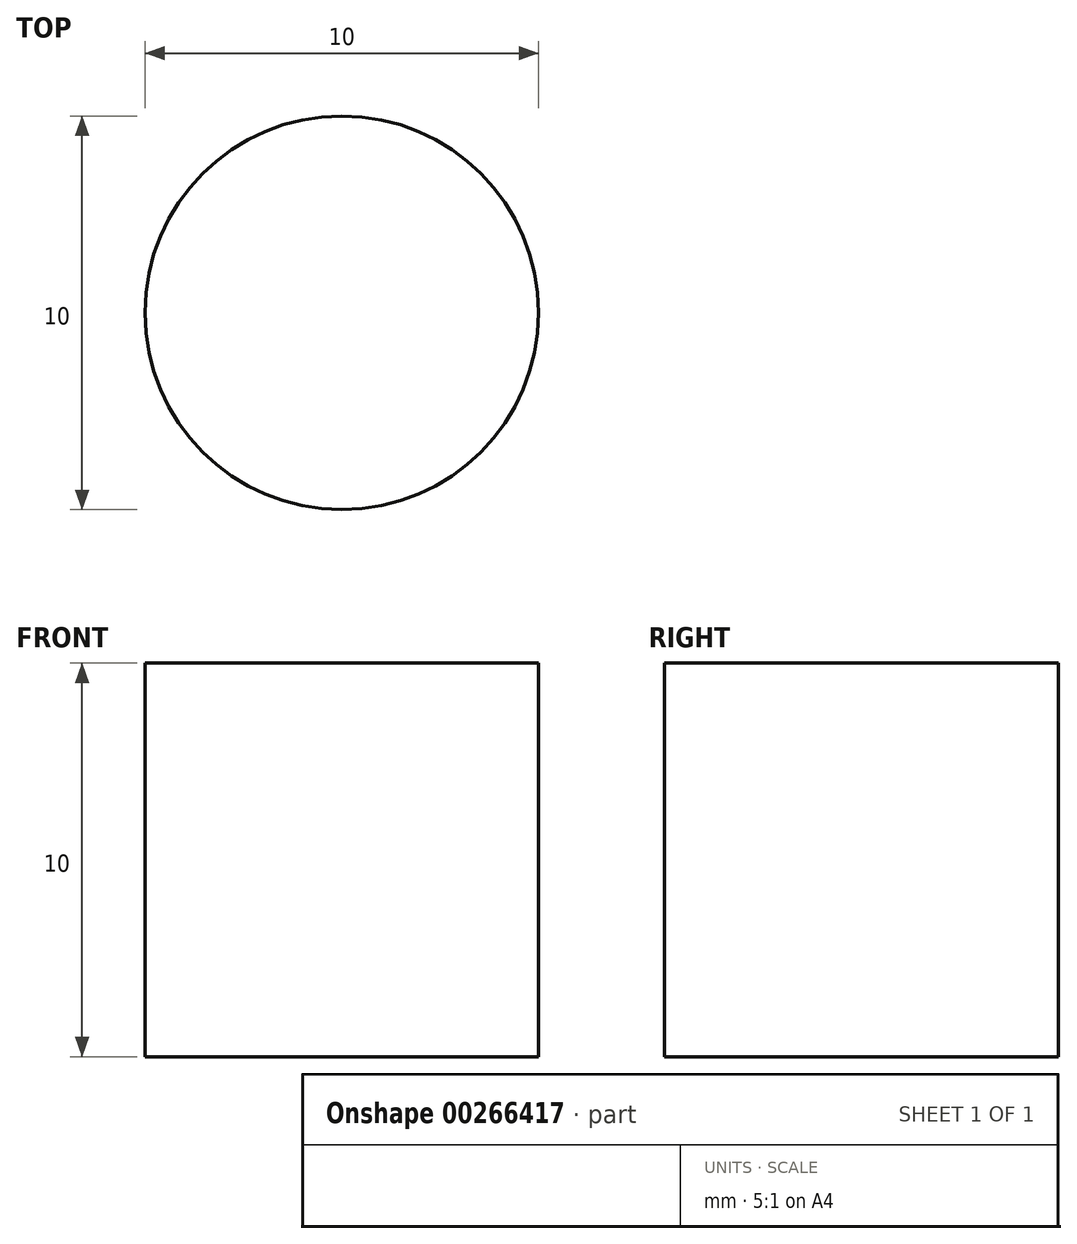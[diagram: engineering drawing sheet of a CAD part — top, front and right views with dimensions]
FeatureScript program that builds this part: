
annotation { "Feature Type Name" : "Feature", "Feature Type Description" : "" }
export const myFeature = defineFeature(function(context is Context, id is Id, definition is map)
    precondition{}
    {
        {
            var Q0;
            Q0=qCreatedBy(makeId("Top.planeOp"),FACE);
            var sketch = newSketch(context, id + "F0", { "sketchPlane" : qUnion([Q0])});
            skCircle(sketch, "E0", {"center": v(0, 0) * mm, "radius": 5 * mm});
            skSolve(sketch);
        }
        {
            var Q0;
            Q0 = qSketchRegion(id + "F0", true);
            extrude(context, id + "F1", {"entities" : qUnion([Q0]), "depth" : 5 * mm, "hasSecondDirection" : true, "secondDirectionOppositeDirection" : true, "secondDirectionDepth" : 5 * mm});
        }
    });
